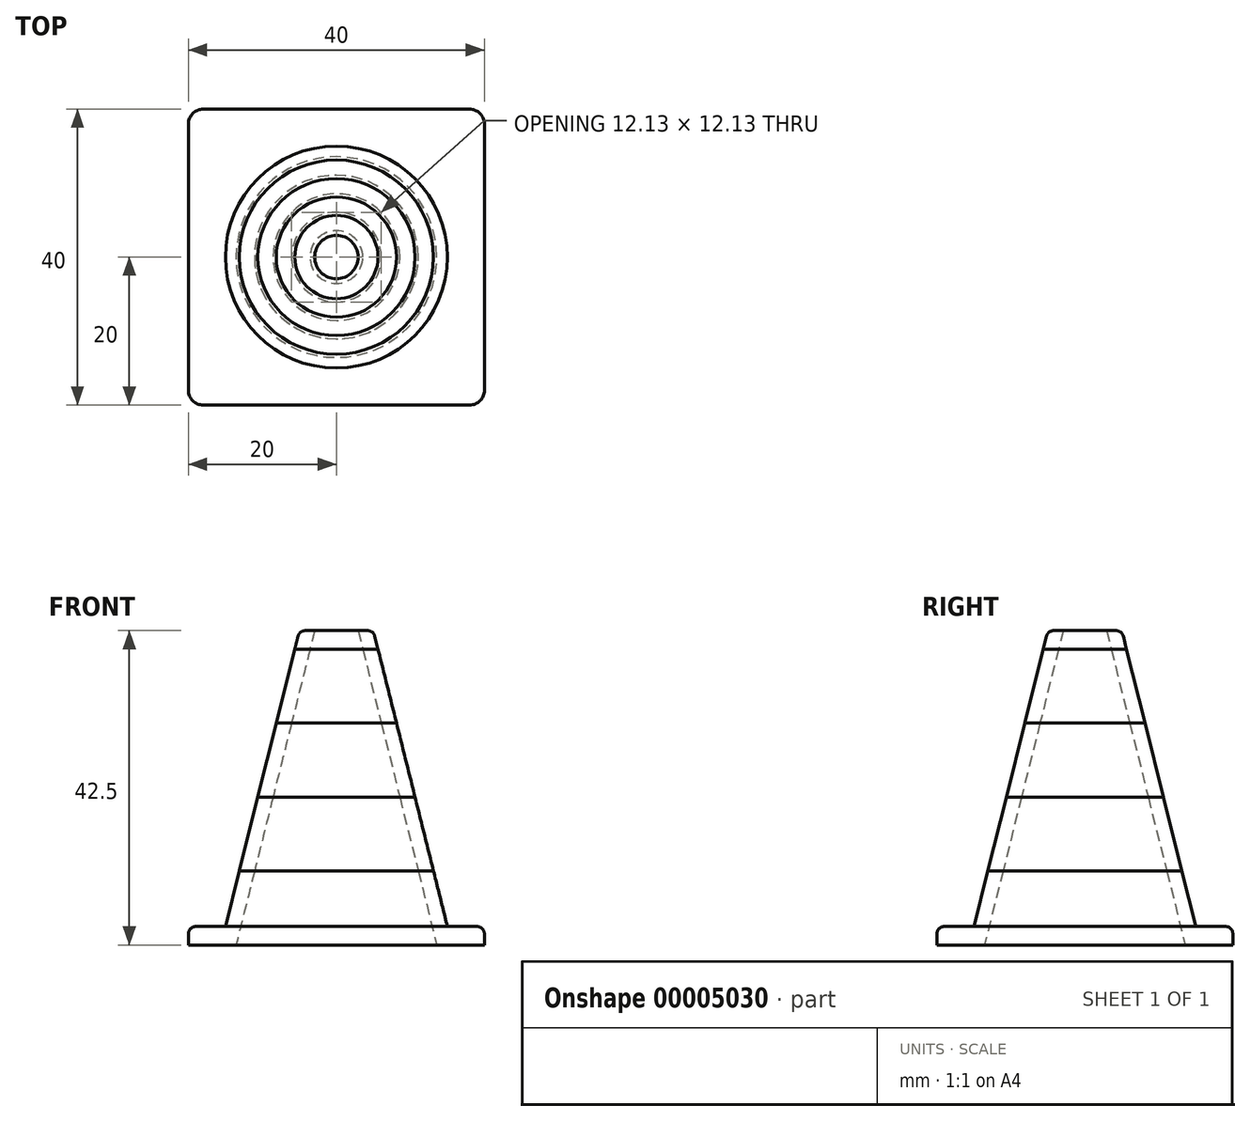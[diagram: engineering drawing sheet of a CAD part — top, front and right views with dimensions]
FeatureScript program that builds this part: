
annotation { "Feature Type Name" : "Feature", "Feature Type Description" : "" }
export const myFeature = defineFeature(function(context is Context, id is Id, definition is map)
    precondition{}
    {
        {
            var Q0;
            Q0=qCreatedBy(makeId("Top.planeOp"),FACE);
            var sketch = newSketch(context, id + "F0", { "sketchPlane" : qUnion([Q0])});
            skLineSegment(sketch, "E0.rect.bottom", {"start": v(-20, -20) * mm, "end": v(20, -20) * mm});
            skLineSegment(sketch, "E0.rect.top", {"start": v(-20, 20) * mm, "end": v(20, 20) * mm});
            skLineSegment(sketch, "E0.rect.left", {"start": v(-20, -20) * mm, "end": v(-20, 20) * mm});
            skLineSegment(sketch, "E0.rect.right", {"start": v(20, -20) * mm, "end": v(20, 20) * mm});
            skPoint(sketch, "E0.rect.middle", {"position": v(0, 0) * mm});
            skSolve(sketch);
        }
        {
            var Q0;
            Q0 = qSketchRegion(id + "F0", true);
            extrude(context, id + "F1", {"entities" : qUnion([Q0]), "depth" : 2.5 * mm});
        }
        {
            var Q0;
            Q0=qCreatedBy(makeId("Right.planeOp"),FACE);
            var sketch = newSketch(context, id + "F2", { "sketchPlane" : qUnion([Q0])});
            skLineSegment(sketch, "E1", {"start": v(0, 42.5) * mm, "end": v(0, 0) * mm, "construction": true});
            skLineSegment(sketch, "E2", {"start": v(-15, 2.5) * mm, "end": v(-5, 42.5) * mm, "construction": true});
            skLineSegment(sketch, "E3", {"start": v(-5, 42.5) * mm, "end": v(0, 42.5) * mm});
            skLineSegment(sketch, "E4", {"start": v(-15, 2.5) * mm, "end": v(-13.13, 10) * mm});
            skLineSegment(sketch, "E5", {"start": v(-13.13, 10) * mm, "end": v(0, 10) * mm});
            skLineSegment(sketch, "E6", {"start": v(0, 10) * mm, "end": v(0, 2.5) * mm});
            skLineSegment(sketch, "E7", {"start": v(0, 2.5) * mm, "end": v(-15, 2.5) * mm});
            skLineSegment(sketch, "E8", {"start": v(-10.63, 20) * mm, "end": v(0, 20) * mm});
            skLineSegment(sketch, "E9", {"start": v(0, 20) * mm, "end": v(0, 30) * mm});
            skLineSegment(sketch, "E10", {"start": v(0, 30) * mm, "end": v(-8.13, 30) * mm});
            skLineSegment(sketch, "E11", {"start": v(-8.13, 30) * mm, "end": v(-10.63, 20) * mm});
            skLineSegment(sketch, "E12", {"start": v(-5, 42.5) * mm, "end": v(-5.63, 40) * mm});
            skLineSegment(sketch, "E13", {"start": v(-5.63, 40) * mm, "end": v(0, 40) * mm});
            skLineSegment(sketch, "E14", {"start": v(0, 40) * mm, "end": v(0, 42.5) * mm});
            skLineSegment(sketch, "E15", {"start": v(-5, 42.5) * mm, "end": v(0, 42.5) * mm, "construction": true});
            skSolve(sketch);
        }
        {
            var Q0;
            Q0 = qSketchRegion(id + "F2", true);
            var Q1;
            Q1=sQuery(id+"F2.wireOp",EDGE,"E1");
            revolve(context, id + "F3", {"operationType" : NewBodyOperationType.ADD, "entities" : qUnion([Q0]), "axis" : qUnion([Q1]), "revolveType" : RevolveType.FULL});
        }
        {
            var Q0;
            Q0=qCreatedBy(makeId("Right.planeOp"),FACE);
            var sketch = newSketch(context, id + "F4", { "sketchPlane" : qUnion([Q0])});
            skLineSegment(sketch, "E16", {"start": v(-13.13, 10) * mm, "end": v(-10.63, 20) * mm});
            skLineSegment(sketch, "E17", {"start": v(-10.63, 20) * mm, "end": v(0, 20) * mm});
            skLineSegment(sketch, "E18", {"start": v(0, 20) * mm, "end": v(0, 10) * mm});
            skLineSegment(sketch, "E19", {"start": v(0, 10) * mm, "end": v(-13.13, 10) * mm});
            skLineSegment(sketch, "E20", {"start": v(-8.12, 30) * mm, "end": v(-5.63, 40) * mm});
            skLineSegment(sketch, "E21", {"start": v(-5.63, 40) * mm, "end": v(0, 40) * mm});
            skLineSegment(sketch, "E22", {"start": v(0, 40) * mm, "end": v(0, 30) * mm});
            skLineSegment(sketch, "E23", {"start": v(0, 30) * mm, "end": v(-8.13, 30) * mm});
            skLineSegment(sketch, "E24", {"start": v(0, 42.88) * mm, "end": v(0, 0) * mm, "construction": true});
            skSolve(sketch);
        }
        {
            var Q0;
            Q0 = qSketchRegion(id + "F4", true);
            var Q1;
            Q1 = qBodyType(qCreatedBy(id + "F4" ,EDGE), BodyType.WIRE);
            var Q2;
            Q2=sQuery(id+"F4.wireOp",EDGE,"E24");
            revolve(context, id + "F5", {"entities" : qUnion([Q0]), "surfaceEntities" : qUnion([Q1]), "axis" : qUnion([Q2]), "revolveType" : RevolveType.FULL});
        }
        {
            var Q0;
            Q0=qCreatedBy(makeId("Right.planeOp"),FACE);
            var sketch = newSketch(context, id + "F6", { "sketchPlane" : qUnion([Q0])});
            skLineSegment(sketch, "E25", {"start": v(0, 0) * mm, "end": v(0, 42.5) * mm, "construction": true});
            skLineSegment(sketch, "E26", {"start": v(-2.94, 42.5) * mm, "end": v(-13.56, 0) * mm});
            skLineSegment(sketch, "E27", {"start": v(-13.56, 0) * mm, "end": v(0, 0) * mm});
            skLineSegment(sketch, "E28", {"start": v(0, 42.5) * mm, "end": v(0, 0) * mm});
            skLineSegment(sketch, "E29", {"start": v(-2.94, 42.5) * mm, "end": v(0, 42.5) * mm});
            skSolve(sketch);
        }
        {
            var Q0;
            Q0 = qSketchRegion(id + "F6", true);
            var Q1;
            Q1=sQuery(id+"F6.wireOp",EDGE,"E28");
            revolve(context, id + "F7", {"operationType" : NewBodyOperationType.REMOVE, "entities" : qUnion([Q0]), "axis" : qUnion([Q1]), "revolveType" : RevolveType.FULL, "oppositeDirection" : true});
        }
        {
            var Q0;
            Q0=makeQuery(id+"F3.opRevolve","SWEPT_EDGE",EDGE,{"disambiguationData":[OSD([sQuery(id+"F2.wireOp",EDGE,"E4"),sQuery(id+"F2.wireOp",EDGE,"E7")])]});
            var Q1;
            Q1=makeQuery(id+"F1.opExtrude","SWEPT_EDGE",EDGE,{"disambiguationData":[OSD([sQuery(id+"F0.wireOp",EDGE,"E0.rect.bottom"),sQuery(id+"F0.wireOp",EDGE,"E0.rect.right")])]});
            var Q2;
            Q2=makeQuery(id+"F1.opExtrude","SWEPT_EDGE",EDGE,{"disambiguationData":[OSD([sQuery(id+"F0.wireOp",EDGE,"E0.rect.top"),sQuery(id+"F0.wireOp",EDGE,"E0.rect.right")])]});
            var Q3;
            Q3=makeQuery(id+"F1.opExtrude","SWEPT_EDGE",EDGE,{"disambiguationData":[OSD([sQuery(id+"F0.wireOp",EDGE,"E0.rect.top"),sQuery(id+"F0.wireOp",EDGE,"E0.rect.left")])]});
            var Q4;
            Q4=makeQuery(id+"F1.opExtrude","SWEPT_EDGE",EDGE,{"disambiguationData":[OSD([sQuery(id+"F0.wireOp",EDGE,"E0.rect.bottom"),sQuery(id+"F0.wireOp",EDGE,"E0.rect.left")])]});
            fillet(context, id + "F8", {"entities" : qUnion([Q0, Q1, Q2, Q3, Q4]), "radius" : 2 * mm, "tangentPropagation" : true, "allowEdgeOverflow" : false});
        }
        {
            var Q0;
            Q0=makeQuery(id+"F3.opRevolve","SWEPT_EDGE",EDGE,{"disambiguationData":[OSD([sQuery(id+"F2.wireOp",EDGE,"E3"),sQuery(id+"F2.wireOp",EDGE,"E12")])]});
            var Q1;
            Q1=makeQuery(id+"F7.boolean.opBoolean","COPY",EDGE,{"derivedFrom":makeQuery(id+"F7.opRevolve","SWEPT_EDGE",EDGE,{"disambiguationData":[OSD([sQuery(id+"F6.wireOp",EDGE,"E26"),sQuery(id+"F6.wireOp",EDGE,"E29")])]})});
            var Q2;
            Q2=makeQuery(id+"F1.opExtrude","CAP_EDGE",EDGE,{"disambiguationData":[OSD([sQuery(id+"F0.wireOp",EDGE,"E0.rect.right")])],"isStart":false});
            var Q3;
            {var subQ0=sQuery(id+"F0.wireOp",EDGE,"E0.rect.bottom");var subQ1=sQuery(id+"F0.wireOp",EDGE,"E0.rect.right");Q3=makeQuery(id+"F8.opFillet","BLEND_EDGE",EDGE,{"blendedFrom":[makeQuery(id+"F1.opExtrude","SWEPT_EDGE",EDGE,{"disambiguationData":[OSD([subQ0,subQ1])]}),makeQuery(id+"F1.opExtrude","CAP_FACE",FACE,{"disambiguationData":[OSD([subQ0,sQuery(id+"F0.wireOp",EDGE,"E0.rect.top"),sQuery(id+"F0.wireOp",EDGE,"E0.rect.left"),subQ1])],"isStart":false})],"blendedInto":[makeQuery(id+"F1.opExtrude","CAP_FACE",FACE,{"disambiguationData":[OSD([subQ0,sQuery(id+"F0.wireOp",EDGE,"E0.rect.top"),sQuery(id+"F0.wireOp",EDGE,"E0.rect.left"),subQ1])],"isStart":false})]});}
            var Q4;
            Q4=makeQuery(id+"F1.opExtrude","CAP_EDGE",EDGE,{"disambiguationData":[OSD([sQuery(id+"F0.wireOp",EDGE,"E0.rect.bottom")])],"isStart":false});
            var Q5;
            {var subQ0=sQuery(id+"F0.wireOp",EDGE,"E0.rect.bottom");var subQ1=sQuery(id+"F0.wireOp",EDGE,"E0.rect.left");Q5=makeQuery(id+"F8.opFillet","BLEND_EDGE",EDGE,{"blendedFrom":[makeQuery(id+"F1.opExtrude","SWEPT_EDGE",EDGE,{"disambiguationData":[OSD([subQ0,subQ1])]}),makeQuery(id+"F1.opExtrude","CAP_FACE",FACE,{"disambiguationData":[OSD([subQ0,sQuery(id+"F0.wireOp",EDGE,"E0.rect.top"),subQ1,sQuery(id+"F0.wireOp",EDGE,"E0.rect.right")])],"isStart":false})],"blendedInto":[makeQuery(id+"F1.opExtrude","CAP_FACE",FACE,{"disambiguationData":[OSD([subQ0,sQuery(id+"F0.wireOp",EDGE,"E0.rect.top"),subQ1,sQuery(id+"F0.wireOp",EDGE,"E0.rect.right")])],"isStart":false})]});}
            var Q6;
            Q6=makeQuery(id+"F1.opExtrude","CAP_EDGE",EDGE,{"disambiguationData":[OSD([sQuery(id+"F0.wireOp",EDGE,"E0.rect.left")])],"isStart":false});
            var Q7;
            {var subQ0=sQuery(id+"F0.wireOp",EDGE,"E0.rect.top");var subQ1=sQuery(id+"F0.wireOp",EDGE,"E0.rect.left");Q7=makeQuery(id+"F8.opFillet","BLEND_EDGE",EDGE,{"blendedFrom":[makeQuery(id+"F1.opExtrude","SWEPT_EDGE",EDGE,{"disambiguationData":[OSD([subQ0,subQ1])]}),makeQuery(id+"F1.opExtrude","CAP_FACE",FACE,{"disambiguationData":[OSD([sQuery(id+"F0.wireOp",EDGE,"E0.rect.bottom"),subQ0,subQ1,sQuery(id+"F0.wireOp",EDGE,"E0.rect.right")])],"isStart":false})],"blendedInto":[makeQuery(id+"F1.opExtrude","CAP_FACE",FACE,{"disambiguationData":[OSD([sQuery(id+"F0.wireOp",EDGE,"E0.rect.bottom"),subQ0,subQ1,sQuery(id+"F0.wireOp",EDGE,"E0.rect.right")])],"isStart":false})]});}
            var Q8;
            Q8=makeQuery(id+"F1.opExtrude","CAP_EDGE",EDGE,{"disambiguationData":[OSD([sQuery(id+"F0.wireOp",EDGE,"E0.rect.top")])],"isStart":false});
            var Q9;
            {var subQ0=sQuery(id+"F0.wireOp",EDGE,"E0.rect.top");var subQ1=sQuery(id+"F0.wireOp",EDGE,"E0.rect.right");Q9=makeQuery(id+"F8.opFillet","BLEND_EDGE",EDGE,{"blendedFrom":[makeQuery(id+"F1.opExtrude","SWEPT_EDGE",EDGE,{"disambiguationData":[OSD([subQ0,subQ1])]}),makeQuery(id+"F1.opExtrude","CAP_FACE",FACE,{"disambiguationData":[OSD([sQuery(id+"F0.wireOp",EDGE,"E0.rect.bottom"),subQ0,sQuery(id+"F0.wireOp",EDGE,"E0.rect.left"),subQ1])],"isStart":false})],"blendedInto":[makeQuery(id+"F1.opExtrude","CAP_FACE",FACE,{"disambiguationData":[OSD([sQuery(id+"F0.wireOp",EDGE,"E0.rect.bottom"),subQ0,sQuery(id+"F0.wireOp",EDGE,"E0.rect.left"),subQ1])],"isStart":false})]});}
            fillet(context, id + "F9", {"entities" : qUnion([Q0, Q1, Q2, Q3, Q4, Q5, Q6, Q7, Q8, Q9]), "radius" : 1 * mm, "tangentPropagation" : true, "allowEdgeOverflow" : false});
        }
    });
